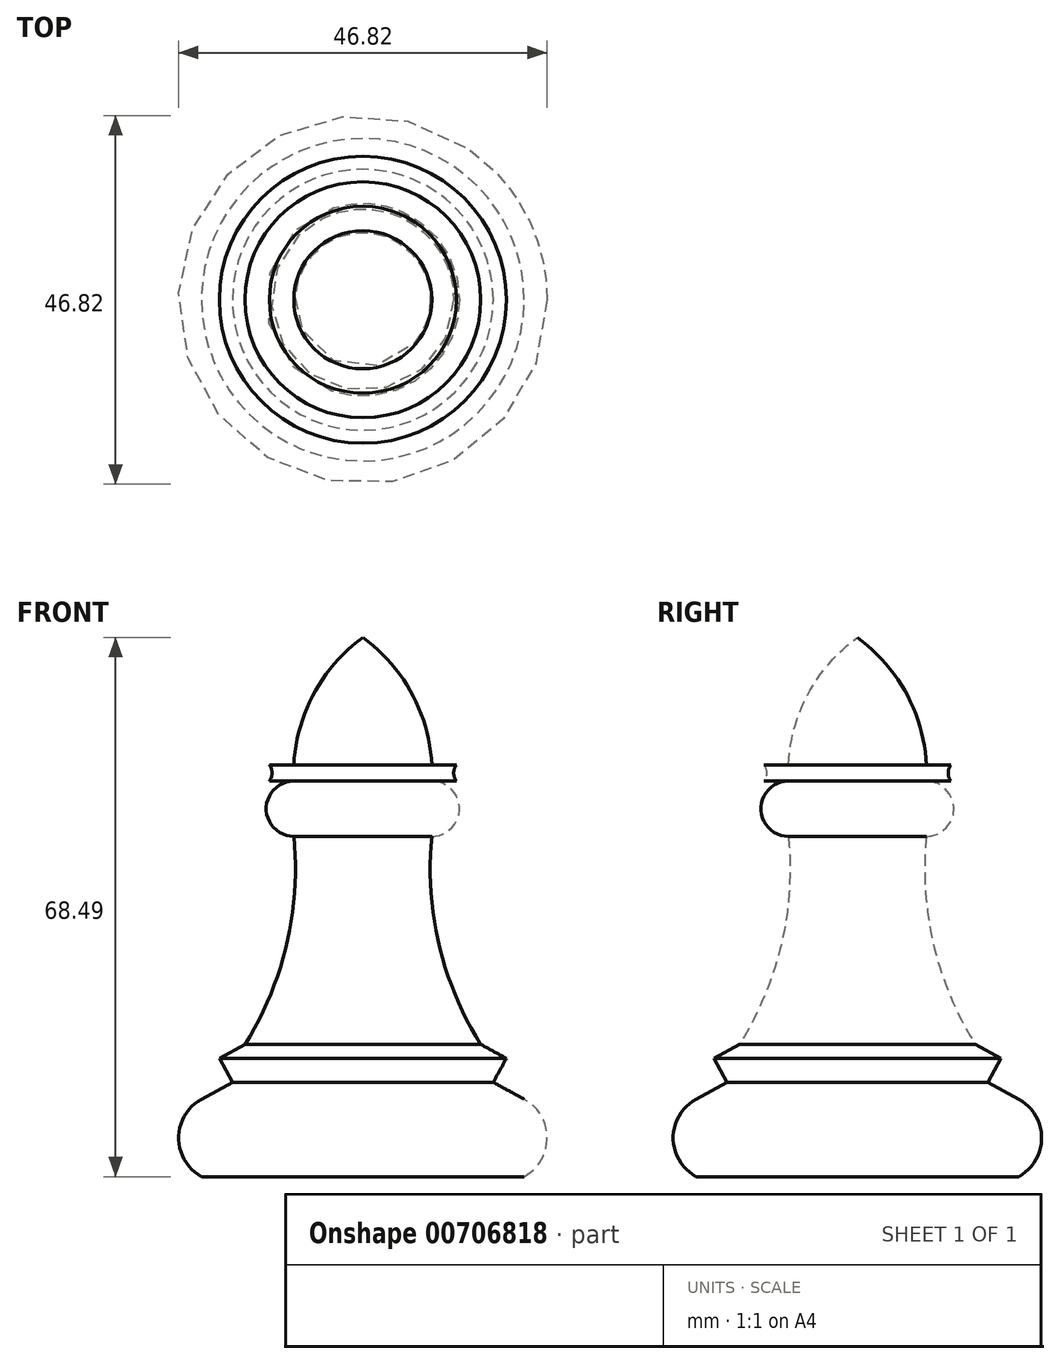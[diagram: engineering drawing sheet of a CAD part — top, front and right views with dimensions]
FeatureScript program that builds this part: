
annotation { "Feature Type Name" : "Feature", "Feature Type Description" : "" }
export const myFeature = defineFeature(function(context is Context, id is Id, definition is map)
    precondition{}
    {
        {
            var Q0;
            Q0=qCreatedBy(makeId("Front.planeOp"),FACE);
            var sketch = newSketch(context, id + "F0", { "sketchPlane" : qUnion([Q0])});
            skLineSegment(sketch, "E0", {"start": v(-20.49, 9.84) * mm, "end": v(-16.57, 11.99) * mm});
            skLineSegment(sketch, "E1", {"start": v(-16.57, 11.99) * mm, "end": v(-18.23, 15.03) * mm});
            skLineSegment(sketch, "E2", {"start": v(-18.23, 15.03) * mm, "end": v(-14.98, 16.8) * mm});
            skLineSegment(sketch, "E3", {"start": v(-8.77, 50.24) * mm, "end": v(-11.87, 50.24) * mm});
            skLineSegment(sketch, "E4", {"start": v(-11.87, 52.33) * mm, "end": v(-8.77, 52.33) * mm});
            skLineSegment(sketch, "E5", {"start": v(0, 62.17) * mm, "end": v(0, 0) * mm});
            skLineSegment(sketch, "E6", {"start": v(0, 0) * mm, "end": v(-20.49, 0) * mm});
            skArc(sketch, "E7", {"start": v(-14.98, 16.8) * mm, "mid": v(-9.67, 29.5) * mm, "end": v(-8.77, 43.24) * mm});
            skArc(sketch, "E8", {"start": v(-11.87, 50.24) * mm, "mid": v(-11.54, 51.29) * mm, "end": v(-11.87, 52.33) * mm});
            skArc(sketch, "E9", {"start": v(-8.77, 50.24) * mm, "mid": v(-12.27, 46.74) * mm, "end": v(-8.77, 43.24) * mm});
            skArc(sketch, "E10", {"start": v(-20.49, 9.84) * mm, "mid": v(-23.4, 4.92) * mm, "end": v(-20.49, 0) * mm});
            skArc(sketch, "E11", {"start": v(0, 68.49) * mm, "mid": v(-6.2, 61.4) * mm, "end": v(-8.77, 52.33) * mm});
            skLineSegment(sketch, "E12", {"start": v(0, 68.49) * mm, "end": v(0, 62.17) * mm});
            skSolve(sketch);
        }
        {
            var Q0;
            Q0=makeQuery(id+"F0.imprint","IMPRINT",FACE,{"disambiguationData":[TD([[makeQuery(id+"F0.imprint","IMPRINT",EDGE,{"derivedFrom":sQuery(id+"F0.wireOp",EDGE,"E0")}),-1.0]])]});
            var Q1;
            Q1=sQuery(id+"F0.wireOp",EDGE,"E5");
            revolve(context, id + "F1", {"surfaceOperationType" : NewSurfaceOperationType.NEW, "entities" : qUnion([Q0]), "axis" : qUnion([Q1]), "revolveType" : RevolveType.FULL});
        }
    });
